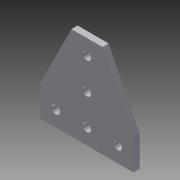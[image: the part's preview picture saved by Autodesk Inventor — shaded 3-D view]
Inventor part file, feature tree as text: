
AUTODESK INVENTOR PART (.ipt)
format: ipt  version: 2014 SP1 (Build 180222100, 222)  size: 90,112 bytes
history: native  units: in
note: dims shown in document units (in); Inventor stores cm internally (conversion verified against a paired STEP export)
features: extrude x1, sketch x1
ambient origin geometry x8: Origin, YZ Plane, XZ Plane, XY Plane, X Axis, Y Axis, Z Axis, Center Point
bodies: Solid1 (feature_tree)
feature tree (2):
  extrude  "Extrusion1"  Depth=0.7874in
  sketch  "Sketch1"  dims[d2=0.7874in d3=0.7874in d4=2.3622in d5=2.3622in d6=0.2047in d8=0.3937in d9=0.7874in d11=0.7874in d12=0.7874in d14=0.7874in d17=1.1811in d19=0.7874in d20=0.3937in d22=1.0in d24=0.1575in d25=0.0in]
